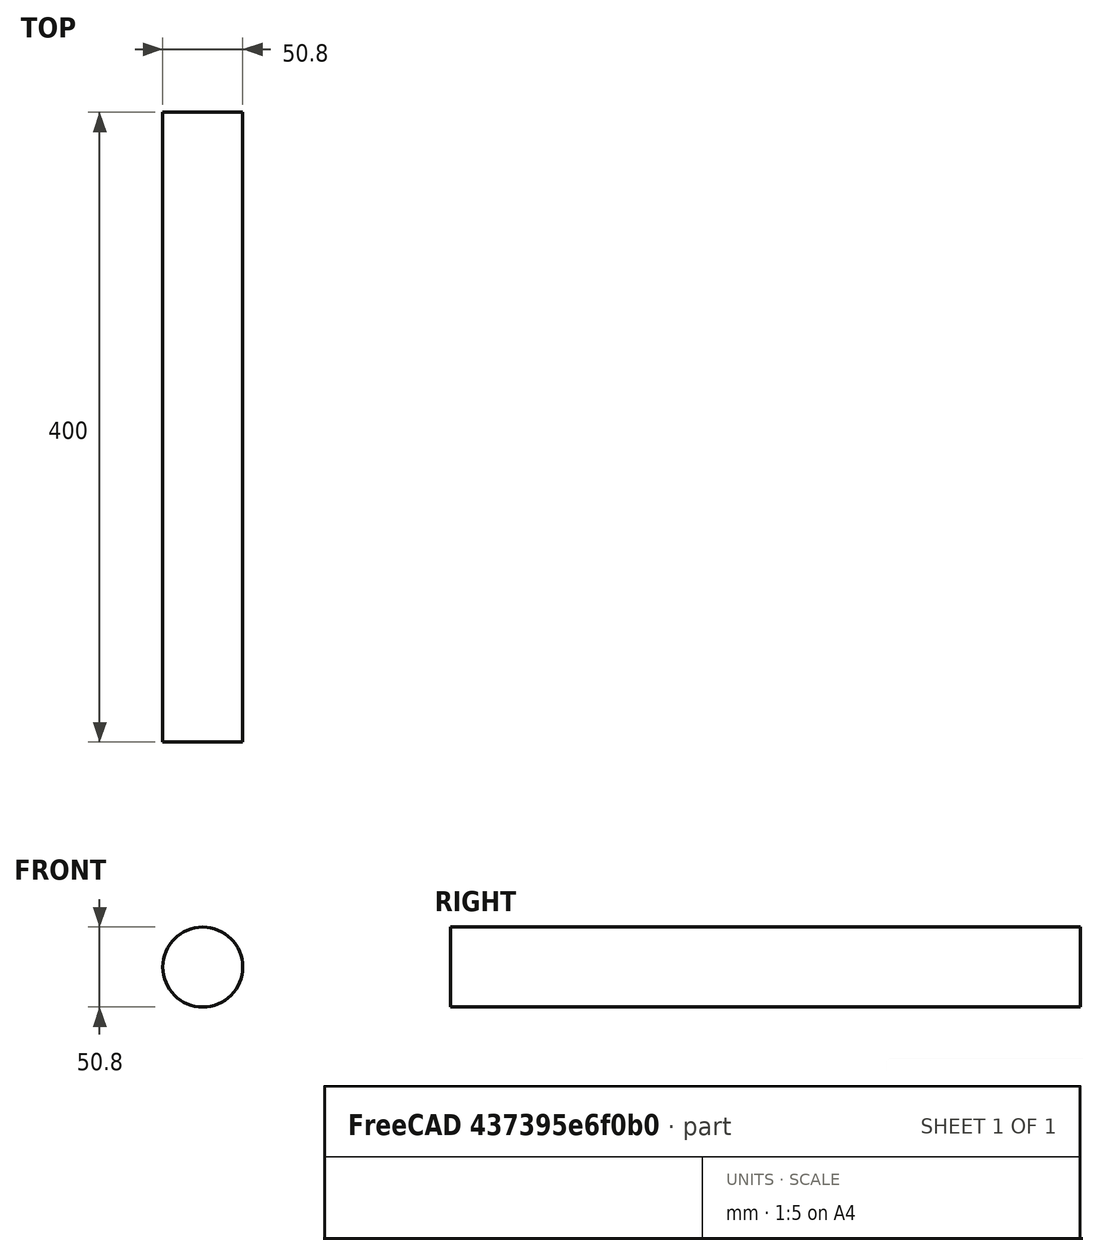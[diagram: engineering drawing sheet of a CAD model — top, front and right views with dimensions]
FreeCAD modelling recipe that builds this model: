
FCSTD DOCUMENT  (FreeCAD 1.0R39109 (Git))
Label: rodillo
License: All rights reserved
LicenseURL: https://en.wikipedia.org/wiki/All_rights_reserved
objects: Sketcher::SketchObject×1, PartDesign::Pad×1, PartDesign::Body×1
note: 6 computed .brp shape members not serialized (recipe doc carries the construction recipe); baked Part::Feature solids carry a one-line shape summary decoded from their .brp

FEATURE [Sketcher::SketchObject] Sketch
  ArcFitTolerance = 1e-06
  AttachmentSupport = -> [XZ_Plane]
  FullyConstrained = true
  MakeInternals = false
  MapMode = 5
  Placement = pos=(0,0,0) rot=(1,0,0;1.5708rad)
  sketch-geometry (1):
    g0: Circle CenterX=0 CenterY=0 CenterZ=0 NormalX=0 NormalY=0 NormalZ=1 AngleXU=0 Radius=25.4
  constraints (2):
    c: Coincident(g0,g-1)
    c: Radius(g0) = 25.4
FEATURE [PartDesign::Pad] Pad
  Direction = (0,-1,2e-16)
  Length = 400
  Length2 = 10
  Placement = pos=(0,0,0) rot=(1,0,0;1.5708rad)
  Profile = -> Sketch [Edge1]
  ReferenceAxis = -> Sketch [N_Axis]
  Refine = true
  Suppressed = false
  Type = 0
FEATURE [PartDesign::Body] Body  label="Cuerpo"
  AllowCompound = false
  Group = -> [Sketch,Pad]
  Origin = -> Origin
  Tip = -> Pad
